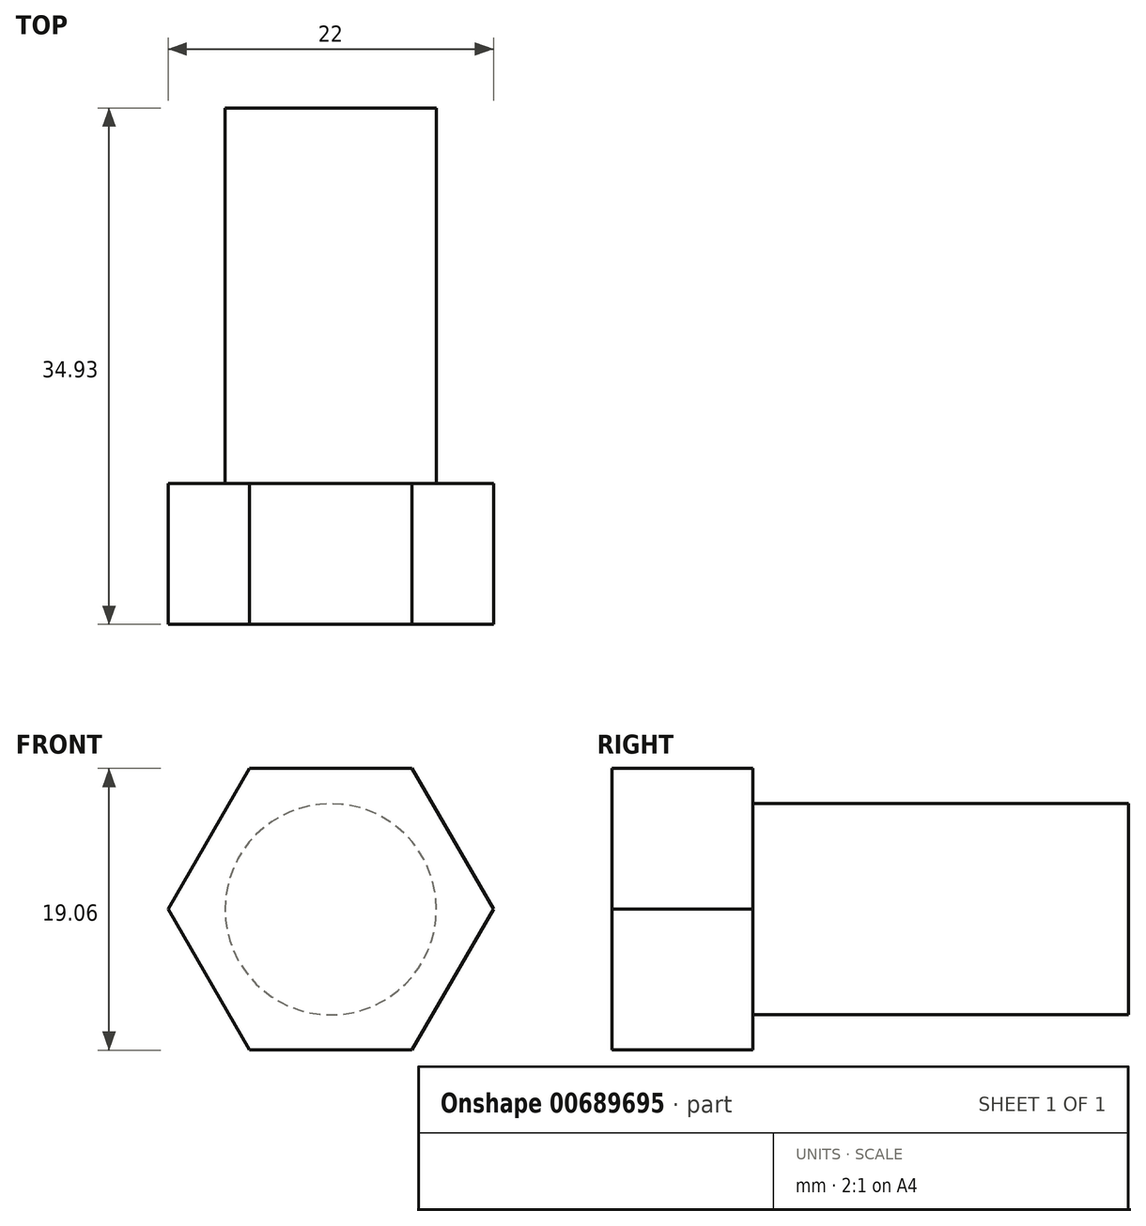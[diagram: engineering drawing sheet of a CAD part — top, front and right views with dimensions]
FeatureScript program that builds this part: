
annotation { "Feature Type Name" : "Feature", "Feature Type Description" : "" }
export const myFeature = defineFeature(function(context is Context, id is Id, definition is map)
    precondition{}
    {
        {
            var Q0;
            Q0=qCreatedBy(makeId("Front.planeOp"),FACE);
            var sketch = newSketch(context, id + "F0", { "sketchPlane" : qUnion([Q0])});
            skCircle(sketch, "E0.cCircle", {"center": v(54.06, 0) * mm, "radius": 9.53 * mm, "construction": true});
            skLineSegment(sketch, "E0.0", {"start": v(48.56, 9.53) * mm, "end": v(59.56, 9.53) * mm});
            skLineSegment(sketch, "E0.1", {"start": v(59.56, 9.53) * mm, "end": v(65.06, 0) * mm});
            skLineSegment(sketch, "E0.2", {"start": v(65.06, 0) * mm, "end": v(59.56, -9.52) * mm});
            skLineSegment(sketch, "E0.3", {"start": v(59.56, -9.52) * mm, "end": v(48.56, -9.53) * mm});
            skLineSegment(sketch, "E0.4", {"start": v(48.56, -9.53) * mm, "end": v(43.06, 0) * mm});
            skLineSegment(sketch, "E0.5", {"start": v(43.06, 0) * mm, "end": v(48.56, 9.53) * mm});
            skPoint(sketch, "E0.0.midPoint", {"position": v(54.06, 9.53) * mm});
            skSolve(sketch);
        }
        {
            var Q0;
            Q0=makeQuery(id+"F0.imprint","IMPRINT",FACE,{"disambiguationData":[TD([[makeQuery(id+"F0.imprint","IMPRINT",EDGE,{"derivedFrom":sQuery(id+"F0.wireOp",EDGE,"E0.0")}),-1.0]])]});
            extrude(context, id + "F1", {"entities" : qUnion([Q0]), "depth" : 9.52 * mm, "offsetDistance" : 25.4 * mm});
        }
        {
            var Q0;
            Q0=makeQuery(id+"F1.opExtrude","CAP_FACE",FACE,{"disambiguationData":[OSD([sQuery(id+"F0.wireOp",EDGE,"E0.0"),sQuery(id+"F0.wireOp",EDGE,"E0.1"),sQuery(id+"F0.wireOp",EDGE,"E0.2"),sQuery(id+"F0.wireOp",EDGE,"E0.3"),sQuery(id+"F0.wireOp",EDGE,"E0.4"),sQuery(id+"F0.wireOp",EDGE,"E0.5")])],"isStart":true});
            var sketch = newSketch(context, id + "F2", { "sketchPlane" : qUnion([Q0])});
            skCircle(sketch, "E1", {"center": v(-54.06, 0) * mm, "radius": 7.14 * mm});
            skPoint(sketch, "E1.centerSnap0", {"position": v(-54.06, 9.53) * mm});
            skSolve(sketch);
        }
        {
            var Q0;
            Q0 = qSketchRegion(id + "F2", true);
            extrude(context, id + "F3", {"entities" : qUnion([Q0]), "operationType" : NewBodyOperationType.ADD, "depth" : 25.4 * mm, "offsetDistance" : 25.4 * mm});
        }
    });
